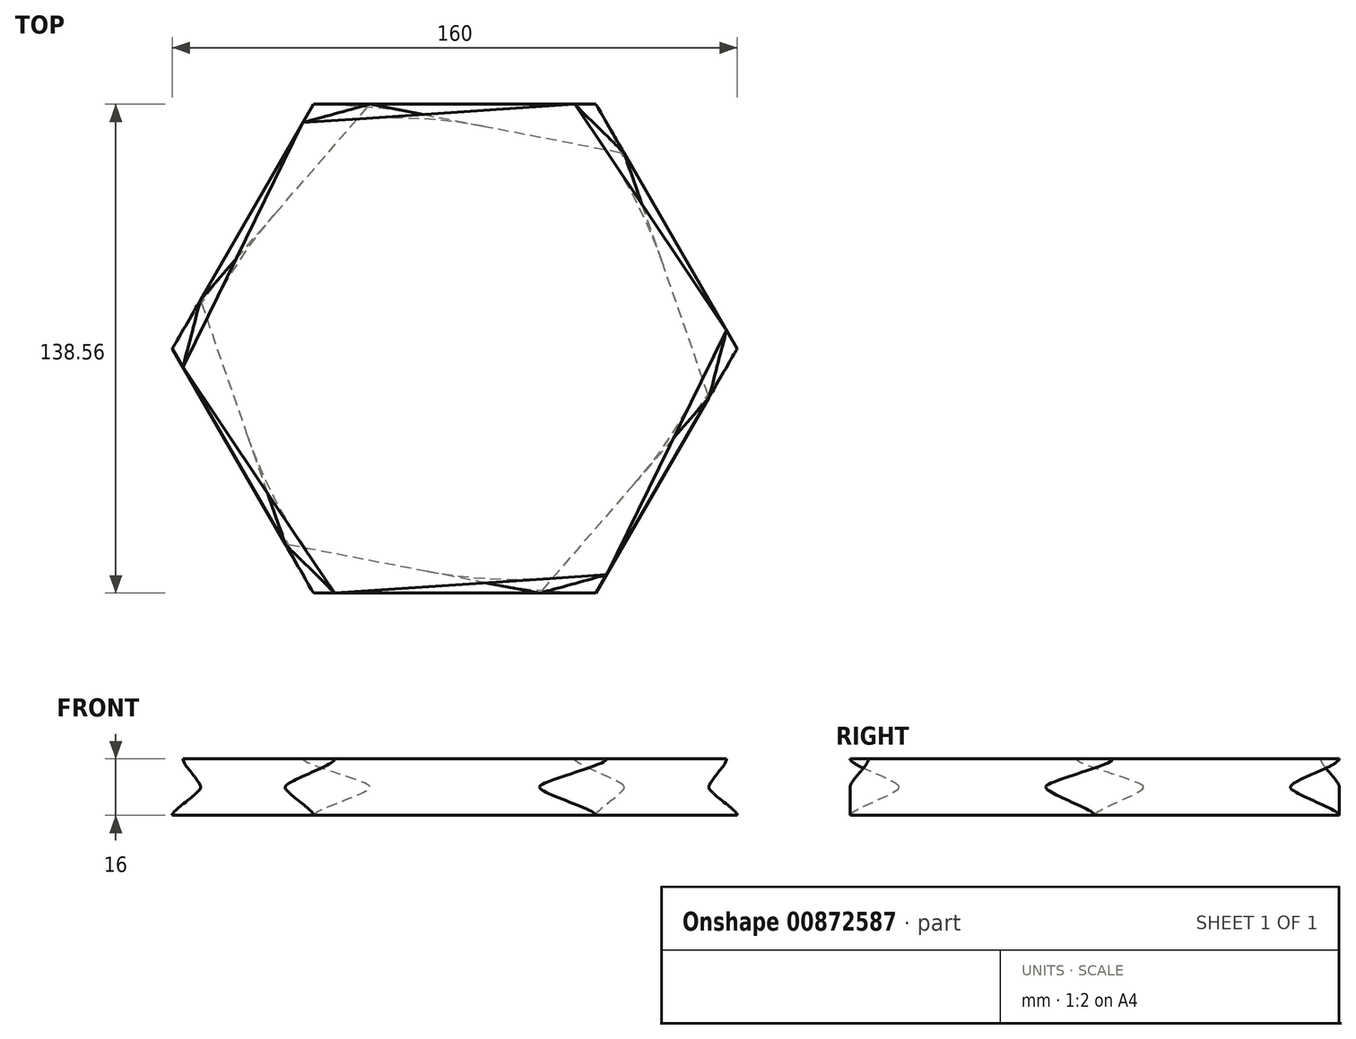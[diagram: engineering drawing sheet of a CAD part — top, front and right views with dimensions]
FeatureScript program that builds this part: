
annotation { "Feature Type Name" : "Feature", "Feature Type Description" : "" }
export const myFeature = defineFeature(function(context is Context, id is Id, definition is map)
    precondition{}
    {
        {
            var Q0;
            Q0=qCreatedBy(makeId("Top.planeOp"),FACE);
            var sketch = newSketch(context, id + "F0", { "sketchPlane" : qUnion([Q0])});
            skCircle(sketch, "E0.cCircle", {"center": v(0, 0) * mm, "radius": 69.28 * mm, "construction": true});
            skLineSegment(sketch, "E0.0", {"start": v(-40, 69.28) * mm, "end": v(40, 69.28) * mm});
            skLineSegment(sketch, "E0.1", {"start": v(40, 69.28) * mm, "end": v(80, 0) * mm});
            skLineSegment(sketch, "E0.2", {"start": v(80, 0) * mm, "end": v(40, -69.28) * mm});
            skLineSegment(sketch, "E0.3", {"start": v(40, -69.28) * mm, "end": v(-40, -69.28) * mm});
            skLineSegment(sketch, "E0.4", {"start": v(-40, -69.28) * mm, "end": v(-80, 0) * mm});
            skLineSegment(sketch, "E0.5", {"start": v(-80, 0) * mm, "end": v(-40, 69.28) * mm});
            skPoint(sketch, "E0.0.midPoint", {"position": v(0, 69.28) * mm});
            skCircle(sketch, "E1.cCircle", {"center": v(0, 0) * mm, "radius": 67.68 * mm, "construction": true});
            skLineSegment(sketch, "E1.0", {"start": v(-39.08, 67.68) * mm, "end": v(39.08, 67.68) * mm, "construction": true});
            skLineSegment(sketch, "E1.1", {"start": v(39.08, 67.68) * mm, "end": v(78.15, 0) * mm, "construction": true});
            skLineSegment(sketch, "E1.2", {"start": v(78.15, 0) * mm, "end": v(39.08, -67.68) * mm, "construction": true});
            skLineSegment(sketch, "E1.3", {"start": v(39.08, -67.68) * mm, "end": v(-39.08, -67.68) * mm, "construction": true});
            skLineSegment(sketch, "E1.4", {"start": v(-39.08, -67.68) * mm, "end": v(-78.15, 0) * mm, "construction": true});
            skLineSegment(sketch, "E1.5", {"start": v(-78.15, 0) * mm, "end": v(-39.08, 67.68) * mm, "construction": true});
            skPoint(sketch, "E1.0.midPoint", {"position": v(0, 67.68) * mm});
            skSolve(sketch);
        }
        {
            var Q0;
            Q0=qCreatedBy(makeId("Top.planeOp"),FACE);
            cPlane(context, id + "F1", {"entities" : qUnion([Q0]), "cplaneType" : CPlaneType.OFFSET, "offset" : 8 * mm, "width" : 150 * mm, "height" : 150 * mm});
        }
        {
            var Q0;
            Q0=qCreatedBy(id+"F1.planeOp",FACE);
            var sketch = newSketch(context, id + "F2", { "sketchPlane" : qUnion([Q0])});
            skCircle(sketch, "E2.cCircle", {"center": v(0, 0) * mm, "radius": 63.5 * mm, "construction": true});
            skLineSegment(sketch, "E2.0", {"start": v(-24, 69.28) * mm, "end": v(48, 55.43) * mm});
            skLineSegment(sketch, "E2.1", {"start": v(48, 55.43) * mm, "end": v(72, -13.86) * mm});
            skLineSegment(sketch, "E2.2", {"start": v(72, -13.86) * mm, "end": v(24, -69.28) * mm});
            skLineSegment(sketch, "E2.3", {"start": v(24, -69.28) * mm, "end": v(-48, -55.43) * mm});
            skLineSegment(sketch, "E2.4", {"start": v(-48, -55.43) * mm, "end": v(-72, 13.86) * mm});
            skLineSegment(sketch, "E2.5", {"start": v(-72, 13.86) * mm, "end": v(-24, 69.28) * mm});
            skPoint(sketch, "E2.0.midPoint", {"position": v(12, 62.35) * mm});
            skCircle(sketch, "E3.cCircle", {"center": v(0, 0) * mm, "radius": 61.9 * mm, "construction": true});
            skLineSegment(sketch, "E3.0", {"start": v(-23.4, 67.54) * mm, "end": v(46.8, 54.03) * mm, "construction": true});
            skLineSegment(sketch, "E3.1", {"start": v(46.8, 54.03) * mm, "end": v(70.19, -13.5) * mm, "construction": true});
            skLineSegment(sketch, "E3.2", {"start": v(70.19, -13.5) * mm, "end": v(23.4, -67.54) * mm, "construction": true});
            skLineSegment(sketch, "E3.3", {"start": v(23.4, -67.54) * mm, "end": v(-46.8, -54.03) * mm, "construction": true});
            skLineSegment(sketch, "E3.4", {"start": v(-46.8, -54.03) * mm, "end": v(-70.19, 13.5) * mm, "construction": true});
            skLineSegment(sketch, "E3.5", {"start": v(-70.19, 13.5) * mm, "end": v(-23.4, 67.54) * mm, "construction": true});
            skPoint(sketch, "E3.0.midPoint", {"position": v(11.7, 60.78) * mm});
            skLineSegment(sketch, "E4", {"start": v(12, 62.35) * mm, "end": v(0, 0) * mm, "construction": true});
            skSolve(sketch);
        }
        {
            var Q0;
            Q0=makeQuery(id+"F0.imprint","IMPRINT",FACE,{"disambiguationData":[TD([[makeQuery(id+"F0.imprint","IMPRINT",EDGE,{"derivedFrom":sQuery(id+"F0.wireOp",EDGE,"E0.0")}),-1.0]])]});
            var Q1;
            Q1=makeQuery(id+"F2.imprint","IMPRINT",FACE,{"disambiguationData":[TD([[makeQuery(id+"F2.imprint","IMPRINT",EDGE,{"derivedFrom":sQuery(id+"F2.wireOp",EDGE,"E2.0")}),-1.0]])]});
            loft(context, id + "F3", {"startCondition" : LoftEndDerivativeType.NORMAL_TO_PROFILE, "startMagnitude" : .6, "endCondition" : LoftEndDerivativeType.NORMAL_TO_PROFILE, "endMagnitude" : .6, "sheetProfilesArray" : [{ "sheetProfileEntities" : qUnion([Q0]) }, { "sheetProfileEntities" : qUnion([Q1]) }]});
        }
        {
            var Q0;
            Q0=qCreatedBy(makeId("Top.planeOp"),FACE);
            cPlane(context, id + "F4", {"entities" : qUnion([Q0]), "cplaneType" : CPlaneType.OFFSET, "offset" : 16 * mm, "width" : 150 * mm, "height" : 150 * mm});
        }
        {
            var Q0;
            Q0=qCreatedBy(id+"F4.planeOp",FACE);
            var sketch = newSketch(context, id + "F5", { "sketchPlane" : qUnion([Q0])});
            skCircle(sketch, "E5.cCircle", {"center": v(0, 0) * mm, "radius": 66.84 * mm, "construction": true});
            skLineSegment(sketch, "E5.0", {"start": v(34, 69.28) * mm, "end": v(77, 5.2) * mm});
            skLineSegment(sketch, "E5.1", {"start": v(77, 5.2) * mm, "end": v(43, -64.09) * mm});
            skLineSegment(sketch, "E5.2", {"start": v(43, -64.09) * mm, "end": v(-34, -69.28) * mm});
            skLineSegment(sketch, "E5.3", {"start": v(-34, -69.28) * mm, "end": v(-77, -5.2) * mm});
            skLineSegment(sketch, "E5.4", {"start": v(-77, -5.2) * mm, "end": v(-43, 64.09) * mm});
            skLineSegment(sketch, "E5.5", {"start": v(-43, 64.09) * mm, "end": v(34, 69.28) * mm});
            skPoint(sketch, "E5.0.midPoint", {"position": v(55.5, 37.24) * mm});
            skSolve(sketch);
        }
        {
            var Q1;
            Q1=makeQuery(id+"F3.opLoft","CAP_FACE",FACE,{"disambiguationData":[OSD([makeQuery(id+"F2.imprint","IMPRINT",FACE,{"disambiguationData":[TD([[makeQuery(id+"F2.imprint","IMPRINT",EDGE,{"derivedFrom":sQuery(id+"F2.wireOp",EDGE,"E2.0")}),-1.0]])]})])],"isStart":true});
            var Q2;
            Q2=makeQuery(id+"F5.imprint","IMPRINT",FACE,{"disambiguationData":[TD([[makeQuery(id+"F5.imprint","IMPRINT",EDGE,{"derivedFrom":sQuery(id+"F5.wireOp",EDGE,"E5.0")}),-1.0]])]});
            loft(context, id + "F6", {"operationType" : NewBodyOperationType.ADD, "startCondition" : LoftEndDerivativeType.NORMAL_TO_PROFILE, "startMagnitude" : .6, "endCondition" : LoftEndDerivativeType.NORMAL_TO_PROFILE, "endMagnitude" : .6, "sheetProfilesArray" : [{ "sheetProfileEntities" : qUnion([Q1]) }, { "sheetProfileEntities" : qUnion([Q2]) }]});
        }
    });
